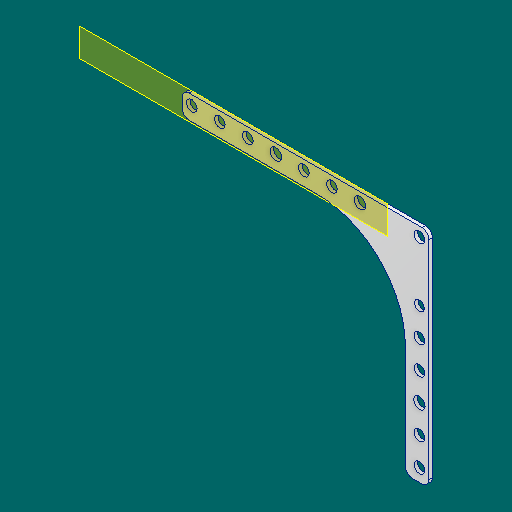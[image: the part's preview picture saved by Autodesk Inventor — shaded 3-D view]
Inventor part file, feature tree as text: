
AUTODESK INVENTOR PART (.ipt)
format: ipt  version: 2023.1 (Build 271208000, 208)  size: 144,896 bytes
history: native  units: in
note: dims shown in document units (in); Inventor stores cm internally (conversion verified against a paired STEP export)
features: other x3, sketch x1, plane x1
ambient origin geometry x8: Origin, YZ Plane, XZ Plane, XY Plane, X Axis, Y Axis, Z Axis, Center Point
bodies: Solid1 (feature_tree)
feature tree (5):
  other  "UnderGusset.ipt"
  other  "Solid1::UnderGusset.ipt"
  other  "TaggingFeature1"
  sketch  "Sketch1"  dims[d0=0.3937in]
  plane  "Work Plane1"
